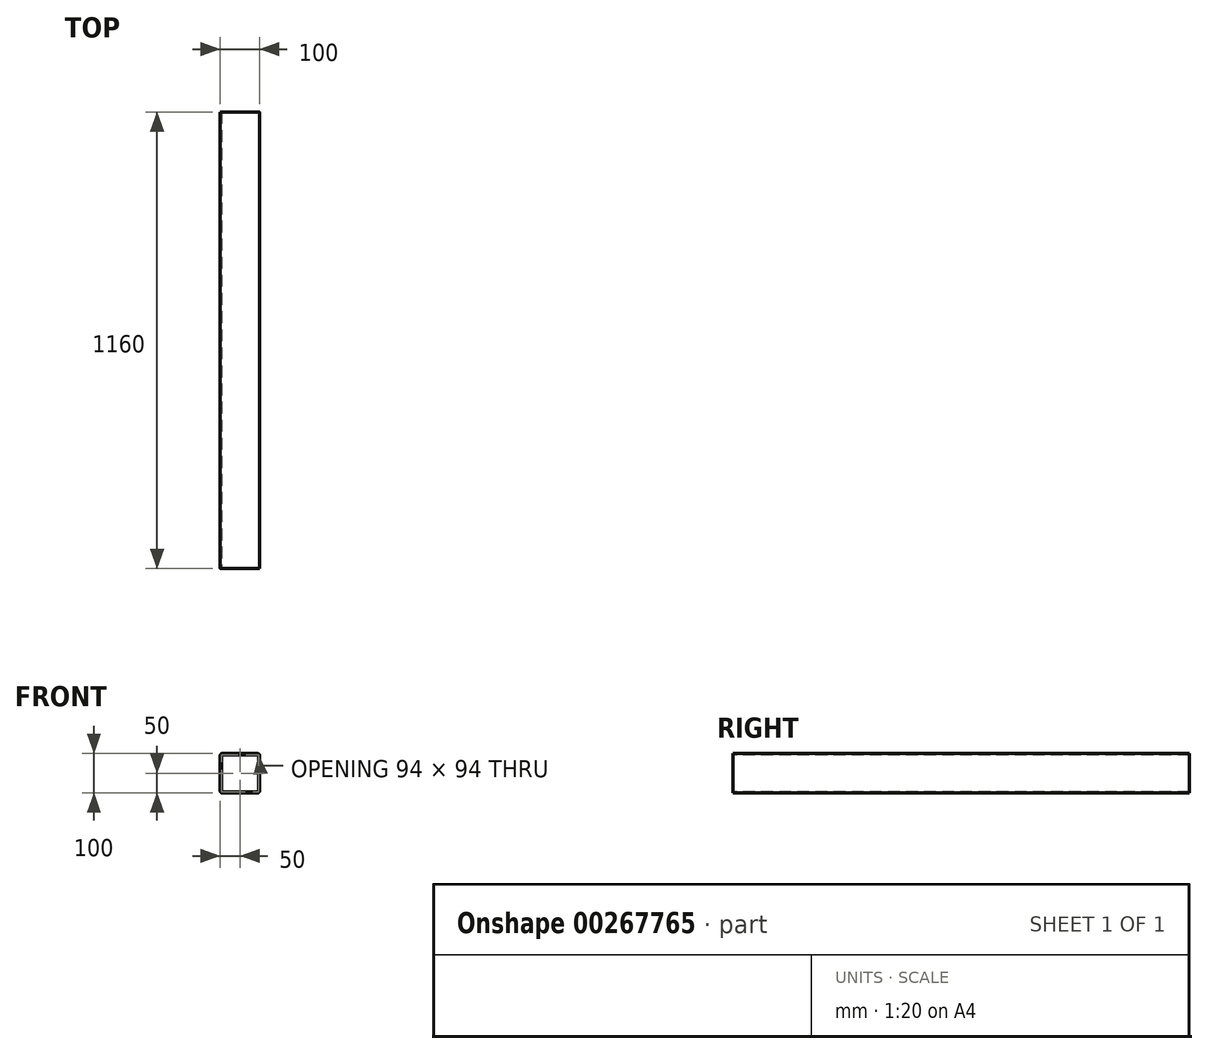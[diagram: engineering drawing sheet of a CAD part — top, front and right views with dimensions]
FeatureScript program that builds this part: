
annotation { "Feature Type Name" : "Feature", "Feature Type Description" : "" }
export const myFeature = defineFeature(function(context is Context, id is Id, definition is map)
    precondition{}
    {
        {
            var Q0;
            Q0=qCreatedBy(makeId("Front.planeOp"),FACE);
            var sketch = newSketch(context, id + "F0", { "sketchPlane" : qUnion([Q0])});
            skLineSegment(sketch, "E0.bottom", {"start": v(45, 50) * mm, "end": v(-45, 50) * mm});
            skLineSegment(sketch, "E0.top", {"start": v(45, -50) * mm, "end": v(-45, -50) * mm});
            skLineSegment(sketch, "E0.left", {"start": v(50, 45) * mm, "end": v(50, -45) * mm});
            skLineSegment(sketch, "E0.right", {"start": v(-50, 45) * mm, "end": v(-50, -45) * mm});
            skPoint(sketch, "E0.middle", {"position": v(0, 0) * mm});
            skPoint(sketch, "E1.visualSharp", {"position": v(-50, 50) * mm});
            skArc(sketch, "E1.filletArc", {"start": v(-45, 50) * mm, "mid": v(-48.54, 48.54) * mm, "end": v(-50, 45) * mm});
            skPoint(sketch, "E2.visualSharp", {"position": v(50, 50) * mm});
            skArc(sketch, "E2.filletArc", {"start": v(50, 45) * mm, "mid": v(48.54, 48.54) * mm, "end": v(45, 50) * mm});
            skPoint(sketch, "E3.visualSharp", {"position": v(50, -50) * mm});
            skArc(sketch, "E3.filletArc", {"start": v(45, -50) * mm, "mid": v(48.54, -48.54) * mm, "end": v(50, -45) * mm});
            skPoint(sketch, "E4.visualSharp", {"position": v(-50, -50) * mm});
            skArc(sketch, "E4.filletArc", {"start": v(-50, -45) * mm, "mid": v(-48.54, -48.54) * mm, "end": v(-45, -50) * mm});
            skArc(sketch, "E5.0", {"start": v(-45, 47) * mm, "mid": v(-46.41, 46.41) * mm, "end": v(-47, 45) * mm});
            skLineSegment(sketch, "E5.1", {"start": v(45, 47) * mm, "end": v(-45, 47) * mm});
            skLineSegment(sketch, "E5.2", {"start": v(-47, 45) * mm, "end": v(-47, -45) * mm});
            skArc(sketch, "E5.3", {"start": v(47, 45) * mm, "mid": v(46.41, 46.41) * mm, "end": v(45, 47) * mm});
            skArc(sketch, "E5.4", {"start": v(-47, -45) * mm, "mid": v(-46.41, -46.41) * mm, "end": v(-45, -47) * mm});
            skLineSegment(sketch, "E5.5", {"start": v(45, -47) * mm, "end": v(-45, -47) * mm});
            skArc(sketch, "E5.6", {"start": v(45, -47) * mm, "mid": v(46.41, -46.41) * mm, "end": v(47, -45) * mm});
            skLineSegment(sketch, "E5.7", {"start": v(47, 45) * mm, "end": v(47, -45) * mm});
            skSolve(sketch);
        }
        {
            var Q0;
            Q0=makeQuery(id+"F0.imprint","IMPRINT",FACE,{"disambiguationData":[TD([[makeQuery(id+"F0.imprint","IMPRINT",EDGE,{"derivedFrom":sQuery(id+"F0.wireOp",EDGE,"E0.bottom")}),1.0]])]});
            extrude(context, id + "F1", {"entities" : qUnion([Q0]), "oppositeDirection" : true, "depth" : 1160 * mm});
        }
    });
